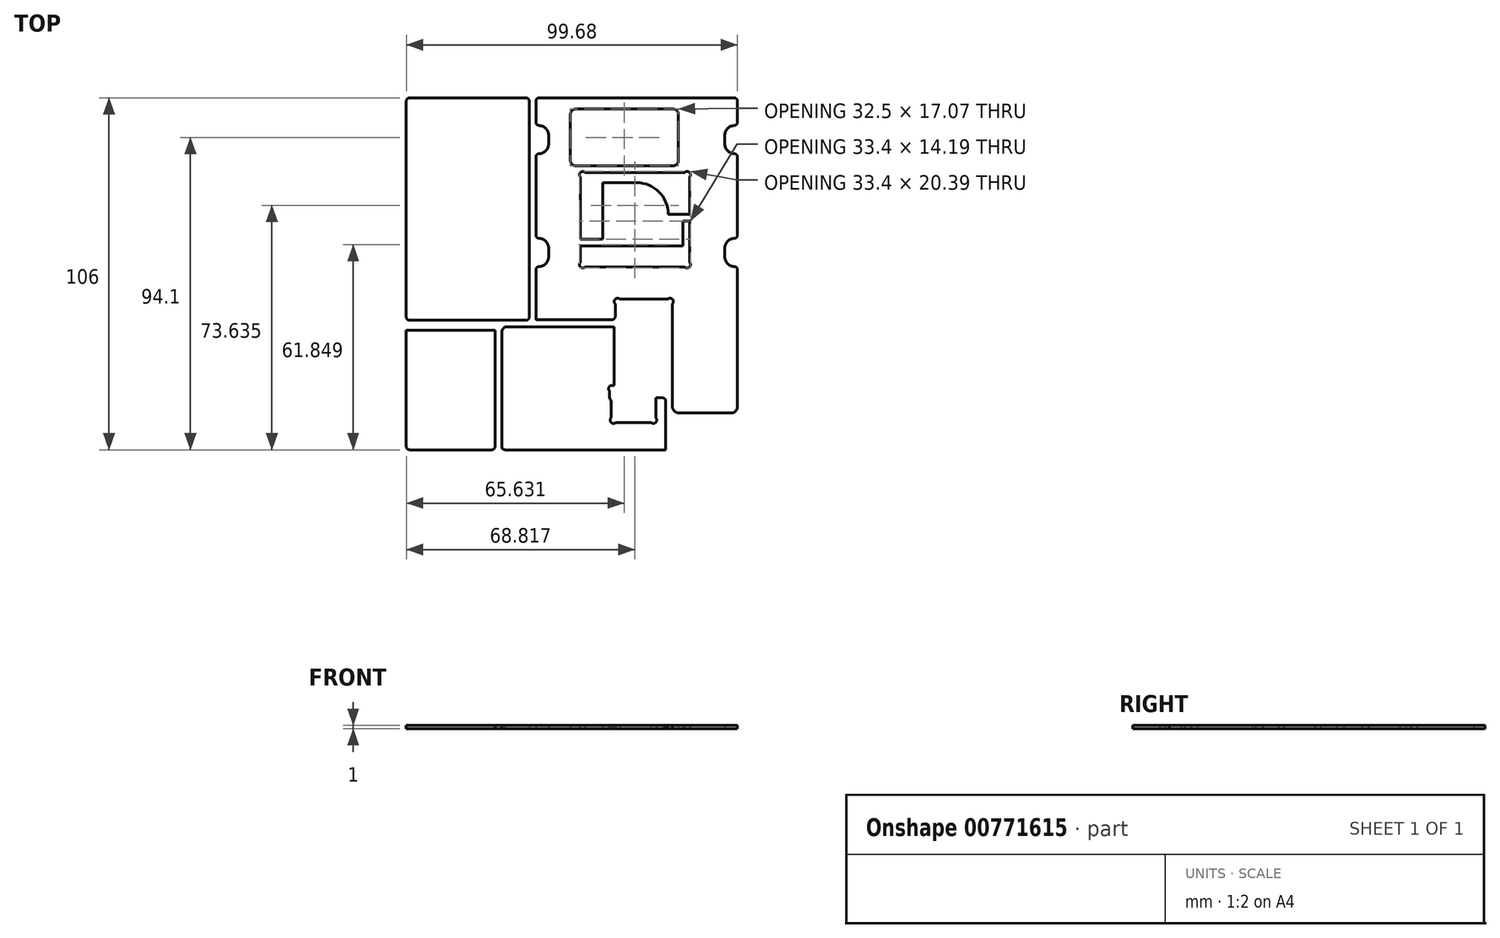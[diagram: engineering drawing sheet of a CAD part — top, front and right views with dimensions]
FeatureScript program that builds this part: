
annotation { "Feature Type Name" : "Feature", "Feature Type Description" : "" }
export const myFeature = defineFeature(function(context is Context, id is Id, definition is map)
    precondition{}
    {
        {
            var Q0;
            Q0=qCreatedBy(makeId("Top.planeOp"),FACE);
            var sketch = newSketch(context, id + "F0", { "sketchPlane" : qUnion([Q0])});
            skLineSegment(sketch, "E0", {"start": v(-24.13, -53) * mm, "end": v(-48.84, -53) * mm});
            skLineSegment(sketch, "E1", {"start": v(-49.84, -52) * mm, "end": v(-49.84, -17) * mm});
            skArc(sketch, "E2", {"start": v(-49.84, -52) * mm, "mid": v(-49.55, -52.7) * mm, "end": v(-48.84, -53) * mm});
            skLineSegment(sketch, "E3", {"start": v(-23.13, -52) * mm, "end": v(-23.13, -17) * mm});
            skArc(sketch, "E4", {"start": v(-24.13, -53) * mm, "mid": v(-23.42, -52.7) * mm, "end": v(-23.13, -52) * mm});
            skArc(sketch, "E5", {"start": v(29, 17.94) * mm, "mid": v(26.22, 24.66) * mm, "end": v(19.5, 27.44) * mm});
            skLineSegment(sketch, "E6", {"start": v(35.39, 17.94) * mm, "end": v(29, 17.94) * mm});
            skLineSegment(sketch, "E7", {"start": v(35.39, 17.94) * mm, "end": v(35.39, 29.12) * mm});
            skLineSegment(sketch, "E8", {"start": v(33.39, 15.94) * mm, "end": v(35.39, 15.94) * mm});
            skLineSegment(sketch, "E9", {"start": v(33.39, 8.44) * mm, "end": v(33.39, 15.94) * mm});
            skLineSegment(sketch, "E10", {"start": v(2.57, 8.44) * mm, "end": v(33.39, 8.44) * mm});
            skLineSegment(sketch, "E11", {"start": v(2.57, 8.44) * mm, "end": v(2.57, 3.46) * mm});
            skLineSegment(sketch, "E12", {"start": v(9.24, 10.44) * mm, "end": v(2.57, 10.44) * mm});
            skLineSegment(sketch, "E13", {"start": v(9.24, 27.44) * mm, "end": v(19.5, 27.44) * mm});
            skLineSegment(sketch, "E14", {"start": v(9.24, 10.44) * mm, "end": v(9.24, 27.44) * mm});
            skLineSegment(sketch, "E15", {"start": v(2.57, 10.44) * mm, "end": v(2.57, 29.12) * mm});
            skLineSegment(sketch, "E16", {"start": v(33.97, 2.05) * mm, "end": v(3.98, 2.05) * mm});
            skLineSegment(sketch, "E17", {"start": v(35.39, 15.94) * mm, "end": v(35.39, 3.46) * mm});
            skLineSegment(sketch, "E18", {"start": v(3.98, 30.53) * mm, "end": v(33.97, 30.53) * mm});
            skArc(sketch, "E19", {"start": v(35.39, 29.12) * mm, "mid": v(35.39, 30.53) * mm, "end": v(33.97, 30.53) * mm});
            skArc(sketch, "E20", {"start": v(3.98, 30.53) * mm, "mid": v(2.57, 30.53) * mm, "end": v(2.57, 29.12) * mm});
            skArc(sketch, "E21", {"start": v(33.97, 2.05) * mm, "mid": v(35.39, 2.05) * mm, "end": v(35.39, 3.46) * mm});
            skArc(sketch, "E22", {"start": v(2.57, 3.46) * mm, "mid": v(2.57, 2.05) * mm, "end": v(3.98, 2.05) * mm});
            skLineSegment(sketch, "E23", {"start": v(-49.84, -4.63) * mm, "end": v(-49.84, -13) * mm});
            skLineSegment(sketch, "E24", {"start": v(-12.84, -13) * mm, "end": v(-12.84, -4.63) * mm});
            skArc(sketch, "E25", {"start": v(-13.84, -14) * mm, "mid": v(-13.14, -13.7) * mm, "end": v(-12.84, -13) * mm});
            skLineSegment(sketch, "E26", {"start": v(-48.84, -14) * mm, "end": v(-13.84, -14) * mm});
            skArc(sketch, "E27", {"start": v(-49.84, -13) * mm, "mid": v(-49.55, -13.7) * mm, "end": v(-48.84, -14) * mm});
            skLineSegment(sketch, "E28", {"start": v(-49.84, -4.63) * mm, "end": v(-49.84, 52) * mm});
            skArc(sketch, "E29", {"start": v(-48.84, 53) * mm, "mid": v(-49.55, 52.7) * mm, "end": v(-49.84, 52) * mm});
            skLineSegment(sketch, "E30", {"start": v(-48.84, 53) * mm, "end": v(-13.84, 53) * mm});
            skArc(sketch, "E31", {"start": v(-12.84, 52) * mm, "mid": v(-13.14, 52.7) * mm, "end": v(-13.84, 53) * mm});
            skLineSegment(sketch, "E32", {"start": v(-12.84, 52) * mm, "end": v(-12.84, -4.63) * mm});
            skArc(sketch, "E33", {"start": v(12.08, -13.81) * mm, "mid": v(12.76, -13.5) * mm, "end": v(13.04, -12.82) * mm});
            skArc(sketch, "E34", {"start": v(30.24, -9.06) * mm, "mid": v(30.24, -7.65) * mm, "end": v(28.83, -7.65) * mm});
            skArc(sketch, "E35", {"start": v(14.45, -7.65) * mm, "mid": v(13.04, -7.65) * mm, "end": v(13.04, -9.06) * mm});
            skArc(sketch, "E36", {"start": v(12.03, -33.6) * mm, "mid": v(11.1, -34.22) * mm, "end": v(11.32, -35.31) * mm});
            skArc(sketch, "E37", {"start": v(23.8, -44.75) * mm, "mid": v(25.22, -44.75) * mm, "end": v(25.22, -43.34) * mm});
            skArc(sketch, "E38", {"start": v(11.82, -43.34) * mm, "mid": v(11.82, -44.75) * mm, "end": v(13.24, -44.75) * mm});
            skArc(sketch, "E39", {"start": v(11.82, -38.35) * mm, "mid": v(11.62, -37.82) * mm, "end": v(11.32, -37.35) * mm});
            skArc(sketch, "E40", {"start": v(28.24, -38.34) * mm, "mid": v(27.95, -37.63) * mm, "end": v(27.24, -37.34) * mm});
            skLineSegment(sketch, "E41", {"start": v(11.32, -37.35) * mm, "end": v(11.32, -35.31) * mm});
            skLineSegment(sketch, "E42", {"start": v(25.22, -37.34) * mm, "end": v(25.22, -43.34) * mm});
            skLineSegment(sketch, "E43", {"start": v(27.28, -37.34) * mm, "end": v(25.22, -37.34) * mm});
            skLineSegment(sketch, "E44", {"start": v(12.72, -16) * mm, "end": v(-20.13, -16) * mm});
            skLineSegment(sketch, "E45", {"start": v(12.72, -33.6) * mm, "end": v(12.72, -16) * mm});
            skLineSegment(sketch, "E46", {"start": v(11.82, -38.35) * mm, "end": v(11.82, -43.34) * mm});
            skLineSegment(sketch, "E47", {"start": v(13.24, -44.75) * mm, "end": v(23.8, -44.75) * mm});
            skLineSegment(sketch, "E48", {"start": v(28.24, -52) * mm, "end": v(28.24, -38.34) * mm});
            skArc(sketch, "E49", {"start": v(-21.13, -52) * mm, "mid": v(-20.83, -52.7) * mm, "end": v(-20.13, -53) * mm});
            skLineSegment(sketch, "E50", {"start": v(-21.13, -17) * mm, "end": v(-21.13, -52) * mm});
            skLineSegment(sketch, "E51", {"start": v(32.24, -41.92) * mm, "end": v(47.84, -41.92) * mm});
            skArc(sketch, "E52", {"start": v(47.84, -41.92) * mm, "mid": v(49.26, -41.33) * mm, "end": v(49.84, -39.92) * mm});
            skLineSegment(sketch, "E53", {"start": v(49.84, -39.92) * mm, "end": v(49.84, 1.19) * mm});
            skArc(sketch, "E54", {"start": v(49.84, 1.19) * mm, "mid": v(49.57, 1.88) * mm, "end": v(48.88, 2.19) * mm});
            skArc(sketch, "E55", {"start": v(46, 5.19) * mm, "mid": v(46.84, 3.1) * mm, "end": v(48.88, 2.19) * mm});
            skLineSegment(sketch, "E56", {"start": v(46, 5.19) * mm, "end": v(46, 7.69) * mm});
            skArc(sketch, "E57", {"start": v(48.88, 10.68) * mm, "mid": v(46.84, 9.76) * mm, "end": v(46, 7.69) * mm});
            skArc(sketch, "E58", {"start": v(48.88, 10.68) * mm, "mid": v(49.56, 10.99) * mm, "end": v(49.84, 11.68) * mm});
            skLineSegment(sketch, "E59", {"start": v(49.84, 11.68) * mm, "end": v(49.84, 35.19) * mm});
            skArc(sketch, "E60", {"start": v(49.84, 35.19) * mm, "mid": v(49.57, 35.88) * mm, "end": v(48.88, 36.19) * mm});
            skArc(sketch, "E61", {"start": v(46, 39.19) * mm, "mid": v(46.84, 37.1) * mm, "end": v(48.88, 36.19) * mm});
            skLineSegment(sketch, "E62", {"start": v(46, 39.19) * mm, "end": v(46, 41.69) * mm});
            skArc(sketch, "E63", {"start": v(48.88, 44.68) * mm, "mid": v(46.84, 43.76) * mm, "end": v(46, 41.69) * mm});
            skArc(sketch, "E64", {"start": v(48.88, 44.68) * mm, "mid": v(49.57, 44.99) * mm, "end": v(49.84, 45.68) * mm});
            skLineSegment(sketch, "E65", {"start": v(49.84, 45.68) * mm, "end": v(49.84, 52) * mm});
            skArc(sketch, "E66", {"start": v(49.84, 52) * mm, "mid": v(49.55, 52.7) * mm, "end": v(48.84, 53) * mm});
            skLineSegment(sketch, "E67", {"start": v(48.84, 53) * mm, "end": v(-9.84, 53) * mm});
            skLineSegment(sketch, "E68", {"start": v(-9.84, -13.81) * mm, "end": v(12.08, -13.81) * mm});
            skLineSegment(sketch, "E69", {"start": v(13.04, -9.06) * mm, "end": v(13.04, -12.82) * mm});
            skLineSegment(sketch, "E70", {"start": v(28.83, -7.65) * mm, "end": v(14.45, -7.65) * mm});
            skLineSegment(sketch, "E71", {"start": v(30.24, -9.06) * mm, "end": v(30.24, -39.92) * mm});
            skArc(sketch, "E72", {"start": v(30.24, -39.92) * mm, "mid": v(30.83, -41.33) * mm, "end": v(32.24, -41.92) * mm});
            skLineSegment(sketch, "E73", {"start": v(30.54, 32.56) * mm, "end": v(1.04, 32.56) * mm});
            skArc(sketch, "E74", {"start": v(-0.46, 34.06) * mm, "mid": v(-0.02, 33) * mm, "end": v(1.04, 32.56) * mm});
            skLineSegment(sketch, "E75", {"start": v(-0.46, 34.06) * mm, "end": v(-0.46, 48.13) * mm});
            skArc(sketch, "E76", {"start": v(1.04, 49.63) * mm, "mid": v(-0.02, 49.2) * mm, "end": v(-0.46, 48.13) * mm});
            skLineSegment(sketch, "E77", {"start": v(1.04, 49.63) * mm, "end": v(30.54, 49.63) * mm});
            skArc(sketch, "E78", {"start": v(32.04, 48.13) * mm, "mid": v(31.6, 49.2) * mm, "end": v(30.54, 49.63) * mm});
            skLineSegment(sketch, "E79", {"start": v(32.04, 48.13) * mm, "end": v(32.04, 34.06) * mm});
            skArc(sketch, "E80", {"start": v(30.54, 32.56) * mm, "mid": v(31.6, 33) * mm, "end": v(32.04, 34.06) * mm});
            skLineSegment(sketch, "E81", {"start": v(-49.84, -17) * mm, "end": v(-23.13, -17) * mm});
            skLineSegment(sketch, "E82", {"start": v(28.24, -52) * mm, "end": v(28.24, -53) * mm});
            skLineSegment(sketch, "E83", {"start": v(12.03, -33.6) * mm, "end": v(12.72, -33.6) * mm});
            skLineSegment(sketch, "E84", {"start": v(-20.13, -16) * mm, "end": v(-21.13, -17) * mm});
            skLineSegment(sketch, "E85", {"start": v(-20.13, -53) * mm, "end": v(28.24, -53) * mm});
            skLineSegment(sketch, "E86", {"start": v(11.82, -43.34) * mm, "end": v(11.82, -38.35) * mm});
            skLineSegment(sketch, "E87", {"start": v(11.82, -38.35) * mm, "end": v(11.32, -37.35) * mm});
            skPoint(sketch, "E88", {"position": v(19.5, 53) * mm});
            skLineSegment(sketch, "E89", {"start": v(19.5, 53) * mm, "end": v(19.5, -7.65) * mm, "construction": true});
            skArc(sketch, "E90.MirrorCS", {"start": v(-7, 39.19) * mm, "mid": v(-7.84, 37.1) * mm, "end": v(-9.88, 36.19) * mm});
            skLineSegment(sketch, "E91.MirrorCS", {"start": v(-7, 39.19) * mm, "end": v(-7, 41.69) * mm});
            skArc(sketch, "E92.MirrorCS", {"start": v(-9.88, 44.68) * mm, "mid": v(-7.84, 43.76) * mm, "end": v(-7, 41.69) * mm});
            skArc(sketch, "E93.MirrorCS", {"start": v(-7, 5.19) * mm, "mid": v(-7.84, 3.1) * mm, "end": v(-9.88, 2.19) * mm});
            skLineSegment(sketch, "E94.MirrorCS", {"start": v(-7, 5.19) * mm, "end": v(-7, 7.69) * mm});
            skArc(sketch, "E95.MirrorCS", {"start": v(-9.88, 10.68) * mm, "mid": v(-7.84, 9.76) * mm, "end": v(-7, 7.69) * mm});
            skArc(sketch, "E96.MirrorCS", {"start": v(-9.88, 10.68) * mm, "mid": v(-10.57, 10.99) * mm, "end": v(-10.84, 11.68) * mm});
            skArc(sketch, "E97.MirrorCS", {"start": v(-10.84, 35.19) * mm, "mid": v(-10.57, 35.88) * mm, "end": v(-9.88, 36.19) * mm});
            skArc(sketch, "E98.MirrorCS", {"start": v(-9.88, 44.68) * mm, "mid": v(-10.57, 44.99) * mm, "end": v(-10.84, 45.68) * mm});
            skArc(sketch, "E99.MirrorCS", {"start": v(-10.84, 1.19) * mm, "mid": v(-10.57, 1.88) * mm, "end": v(-9.88, 2.19) * mm});
            skArc(sketch, "E100.MirrorCS", {"start": v(-10.84, 52) * mm, "mid": v(-10.55, 52.7) * mm, "end": v(-9.84, 53) * mm});
            skLineSegment(sketch, "E101.MirrorCS", {"start": v(-10.84, 11.68) * mm, "end": v(-10.84, 35.19) * mm});
            skLineSegment(sketch, "E102.MirrorCS", {"start": v(-10.84, 45.68) * mm, "end": v(-10.84, 52) * mm});
            skLineSegment(sketch, "E103", {"start": v(-10.84, 1.19) * mm, "end": v(-10.84, -13.57) * mm});
            skLineSegment(sketch, "E104", {"start": v(-9.84, -13.81) * mm, "end": v(-10.6, -13.81) * mm});
            skPoint(sketch, "E105.visualSharp", {"position": v(-10.84, -13.81) * mm});
            skArc(sketch, "E105.filletArc", {"start": v(-10.84, -13.57) * mm, "mid": v(-10.77, -13.74) * mm, "end": v(-10.6, -13.81) * mm});
            skSolve(sketch);
        }
        {
            var Q0;
            Q0=makeQuery(id+"F0.imprint","IMPRINT",FACE,{"disambiguationData":[TD([[makeQuery(id+"F0.imprint","IMPRINT",EDGE,{"derivedFrom":sQuery(id+"F0.wireOp",EDGE,"E23")}),1.0]])]});
            var Q1;
            Q1=makeQuery(id+"F0.imprint","IMPRINT",FACE,{"disambiguationData":[TD([[makeQuery(id+"F0.imprint","IMPRINT",EDGE,{"derivedFrom":sQuery(id+"F0.wireOp",EDGE,"E0")}),-1.0]])]});
            var Q2;
            Q2=makeQuery(id+"F0.imprint","IMPRINT",FACE,{"disambiguationData":[TD([[makeQuery(id+"F0.imprint","IMPRINT",EDGE,{"derivedFrom":sQuery(id+"F0.wireOp",EDGE,"E36")}),-1.0]])]});
            var Q3;
            Q3=makeQuery(id+"F0.imprint","IMPRINT",FACE,{"disambiguationData":[TD([[makeQuery(id+"F0.imprint","IMPRINT",EDGE,{"derivedFrom":sQuery(id+"F0.wireOp",EDGE,"E5")}),1.0]])]});
            extrude(context, id + "F1", {"entities" : qUnion([Q0, Q1, Q2, Q3]), "depth" : 1 * mm, "offsetDistance" : 25 * mm});
        }
    });
